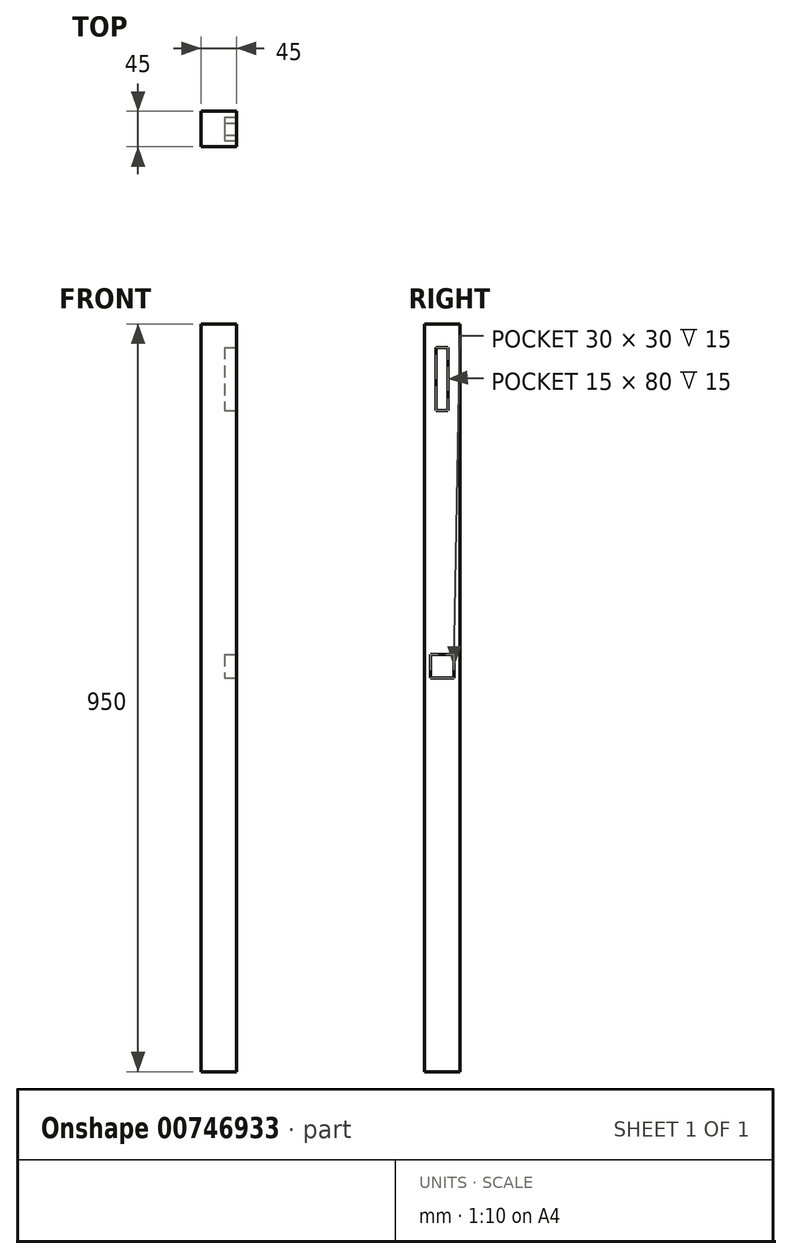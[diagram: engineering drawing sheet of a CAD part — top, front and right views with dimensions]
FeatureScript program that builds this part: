
annotation { "Feature Type Name" : "Feature", "Feature Type Description" : "" }
export const myFeature = defineFeature(function(context is Context, id is Id, definition is map)
    precondition{}
    {
        {
            var Q0;
            Q0=qCreatedBy(makeId("Top.planeOp"),FACE);
            var sketch = newSketch(context, id + "F0", { "sketchPlane" : qUnion([Q0])});
            skLineSegment(sketch, "E0.bottom", {"start": v(22.5, 22.5) * mm, "end": v(-22.5, 22.5) * mm});
            skLineSegment(sketch, "E0.top", {"start": v(22.5, -22.5) * mm, "end": v(-22.5, -22.5) * mm});
            skLineSegment(sketch, "E0.left", {"start": v(22.5, 22.5) * mm, "end": v(22.5, -22.5) * mm});
            skLineSegment(sketch, "E0.right", {"start": v(-22.5, 22.5) * mm, "end": v(-22.5, -22.5) * mm});
            skPoint(sketch, "E0.middle", {"position": v(0, 0) * mm});
            skSolve(sketch);
        }
        {
            var Q0;
            Q0 = qSketchRegion(id + "F0", true);
            extrude(context, id + "F1", {"entities" : qUnion([Q0]), "endBound" : BoundingType.SYMMETRIC, "depth" : 950 * mm, "offsetDistance" : 25 * mm});
        }
        {
            var Q0;
            Q0=makeQuery(id+"F1.opExtrude","SWEPT_FACE",FACE,{"disambiguationData":[OSD([sQuery(id+"F0.wireOp",EDGE,"E0.left")])]});
            var sketch = newSketch(context, id + "F2", { "sketchPlane" : qUnion([Q0])});
            skLineSegment(sketch, "E1.bottom", {"start": v(7.5, 445) * mm, "end": v(-7.5, 445) * mm});
            skLineSegment(sketch, "E1.top", {"start": v(7.5, 365) * mm, "end": v(-7.5, 365) * mm});
            skLineSegment(sketch, "E1.left", {"start": v(7.5, 445) * mm, "end": v(7.5, 365) * mm});
            skLineSegment(sketch, "E1.right", {"start": v(-7.5, 445) * mm, "end": v(-7.5, 365) * mm});
            skPoint(sketch, "E1.middle", {"position": v(0, 405) * mm});
            skLineSegment(sketch, "E2.bottom", {"start": v(15, 55) * mm, "end": v(-15, 55) * mm});
            skLineSegment(sketch, "E2.top", {"start": v(15, 25) * mm, "end": v(-15, 25) * mm});
            skLineSegment(sketch, "E2.left", {"start": v(15, 55) * mm, "end": v(15, 25) * mm});
            skLineSegment(sketch, "E2.right", {"start": v(-15, 55) * mm, "end": v(-15, 25) * mm});
            skPoint(sketch, "E2.middle", {"position": v(0, 40) * mm});
            skSolve(sketch);
        }
        {
            var Q0;
            Q0 = qSketchRegion(id + "F2", true);
            extrude(context, id + "F3", {"entities" : qUnion([Q0]), "operationType" : NewBodyOperationType.REMOVE, "oppositeDirection" : true, "depth" : 15 * mm, "offsetDistance" : 25 * mm});
        }
    });
